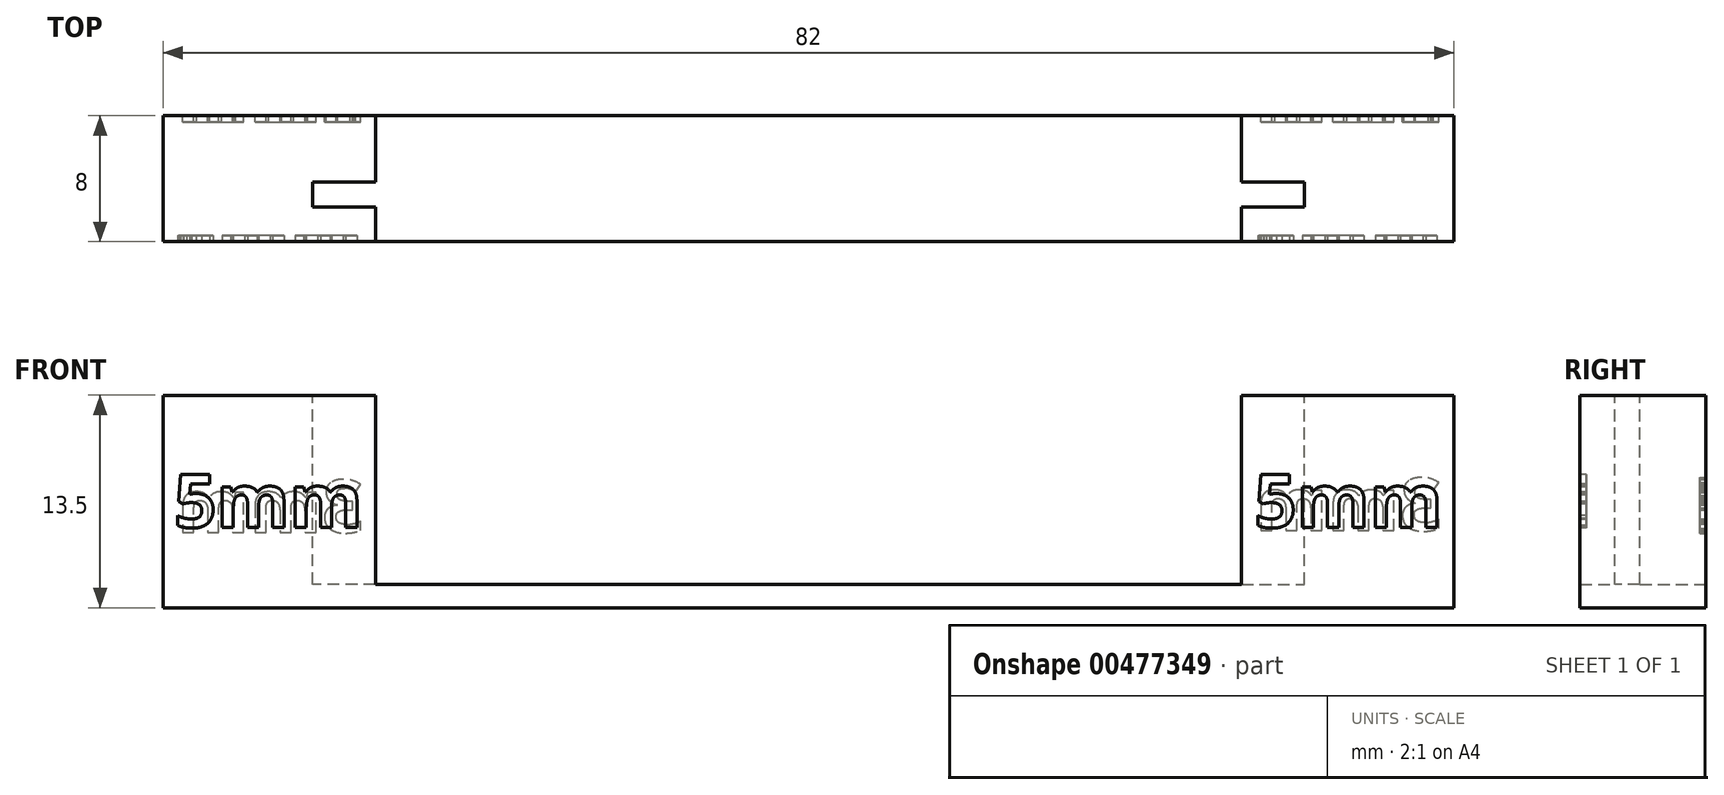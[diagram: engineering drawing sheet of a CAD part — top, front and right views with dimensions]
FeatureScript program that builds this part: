
annotation { "Feature Type Name" : "Feature", "Feature Type Description" : "" }
export const myFeature = defineFeature(function(context is Context, id is Id, definition is map)
    precondition{}
    {
        {
            var Q0;
            Q0=qCreatedBy(makeId("Front.planeOp"),FACE);
            var sketch = newSketch(context, id + "F0", { "sketchPlane" : qUnion([Q0])});
            skLineSegment(sketch, "E0.bottom", {"start": v(-137.41, 25.8) * mm, "end": v(-123.91, 25.8) * mm});
            skLineSegment(sketch, "E0.top", {"start": v(-137.41, 12.3) * mm, "end": v(-123.91, 12.3) * mm});
            skLineSegment(sketch, "E0.left", {"start": v(-137.41, 25.8) * mm, "end": v(-137.41, 12.3) * mm});
            skLineSegment(sketch, "E0.right", {"start": v(-123.91, 25.8) * mm, "end": v(-123.91, 12.3) * mm});
            skLineSegment(sketch, "E1.bottom", {"start": v(-123.91, 12.3) * mm, "end": v(-68.91, 12.3) * mm});
            skLineSegment(sketch, "E1.top", {"start": v(-123.91, 13.8) * mm, "end": v(-68.91, 13.8) * mm});
            skLineSegment(sketch, "E1.left", {"start": v(-123.91, 12.3) * mm, "end": v(-123.91, 13.8) * mm});
            skLineSegment(sketch, "E1.right", {"start": v(-68.91, 12.3) * mm, "end": v(-68.91, 13.8) * mm});
            skLineSegment(sketch, "E2.bottom", {"start": v(-68.91, 12.3) * mm, "end": v(-55.41, 12.3) * mm});
            skLineSegment(sketch, "E2.top", {"start": v(-68.91, 25.8) * mm, "end": v(-55.41, 25.8) * mm});
            skLineSegment(sketch, "E2.left", {"start": v(-68.91, 12.3) * mm, "end": v(-68.91, 25.8) * mm});
            skLineSegment(sketch, "E2.right", {"start": v(-55.41, 12.3) * mm, "end": v(-55.41, 25.8) * mm});
            skSolve(sketch);
        }
        {
            var Q0;
            Q0 = qSketchRegion(id + "F0", true);
            extrude(context, id + "F1", {"entities" : qUnion([Q0]), "depth" : 8 * mm});
        }
        {
            var Q0;
            Q0=makeQuery(id+"F1.opExtrude","SWEPT_FACE",FACE,{"disambiguationData":[OSD([sQuery(id+"F0.wireOp",EDGE,"E0.bottom")])]});
            var sketch = newSketch(context, id + "F2", { "sketchPlane" : qUnion([Q0])});
            skLineSegment(sketch, "E3.bottom", {"start": v(-123.91, -4.2) * mm, "end": v(-127.91, -4.2) * mm});
            skLineSegment(sketch, "E3.top", {"start": v(-123.91, -5.8) * mm, "end": v(-127.91, -5.8) * mm});
            skLineSegment(sketch, "E3.left", {"start": v(-123.91, -4.2) * mm, "end": v(-123.91, -5.8) * mm});
            skLineSegment(sketch, "E3.right", {"start": v(-127.91, -4.2) * mm, "end": v(-127.91, -5.8) * mm});
            skSolve(sketch);
        }
        {
            var Q0;
            Q0=makeQuery(id+"F2.imprint","IMPRINT",FACE,{"disambiguationData":[TD([[makeQuery(id+"F2.imprint","IMPRINT",EDGE,{"derivedFrom":sQuery(id+"F2.wireOp",EDGE,"E3.bottom")}),1.0]])]});
            extrude(context, id + "F3", {"entities" : qUnion([Q0]), "operationType" : NewBodyOperationType.REMOVE, "oppositeDirection" : true, "depth" : 12 * mm});
        }
        {
            var Q0;
            Q0=makeQuery(id+"F1.opExtrude","SWEPT_FACE",FACE,{"disambiguationData":[OSD([sQuery(id+"F0.wireOp",EDGE,"E2.top")])]});
            var sketch = newSketch(context, id + "F4", { "sketchPlane" : qUnion([Q0])});
            skLineSegment(sketch, "E4.bottom", {"start": v(-68.91, -4.2) * mm, "end": v(-64.91, -4.2) * mm});
            skLineSegment(sketch, "E4.top", {"start": v(-68.91, -5.8) * mm, "end": v(-64.91, -5.8) * mm});
            skLineSegment(sketch, "E4.left", {"start": v(-68.91, -4.2) * mm, "end": v(-68.91, -5.8) * mm});
            skLineSegment(sketch, "E4.right", {"start": v(-64.91, -4.2) * mm, "end": v(-64.91, -5.8) * mm});
            skSolve(sketch);
        }
        {
            var Q0;
            Q0 = qSketchRegion(id + "F4", true);
            extrude(context, id + "F5", {"entities" : qUnion([Q0]), "operationType" : NewBodyOperationType.REMOVE, "oppositeDirection" : true, "depth" : 12 * mm});
        }
        {
            var Q0;
            Q0=makeQuery(id+"F1.opExtrude","CAP_FACE",FACE,{"disambiguationData":[OSD([sQuery(id+"F0.wireOp",EDGE,"E0.bottom"),sQuery(id+"F0.wireOp",EDGE,"E0.top"),sQuery(id+"F0.wireOp",EDGE,"E0.left"),sQuery(id+"F0.wireOp",EDGE,"E0.right"),sQuery(id+"F0.wireOp",EDGE,"E1.bottom"),sQuery(id+"F0.wireOp",EDGE,"E1.top"),sQuery(id+"F0.wireOp",EDGE,"E2.bottom"),sQuery(id+"F0.wireOp",EDGE,"E2.top"),sQuery(id+"F0.wireOp",EDGE,"E2.left"),sQuery(id+"F0.wireOp",EDGE,"E2.right")])],"isStart":true});
            var sketch = newSketch(context, id + "F6", { "sketchPlane" : qUnion([Q0])});
            skText(sketch, "E5", { "text": "3mm", "fontName": "OpenSans-Bold.ttf"});
            skText(sketch, "E6", { "text": "3mm", "fontName": "OpenSans-Bold.ttf"});
            const initialGuessF6  = {"E5": [0.0562, 0.0172, 1, 0, 0.00336], "E6": [0.12467, 0.01708, 1, 0, 0.00336]};
            skSetInitialGuess(sketch, initialGuessF6);
            skSolve(sketch);
        }
        {
            var Q0;
            Q0 = qSketchRegion(id + "F6", true);
            extrude(context, id + "F7", {"entities" : qUnion([Q0]), "operationType" : NewBodyOperationType.REMOVE, "oppositeDirection" : true, "depth" : 0.4 * mm});
        }
        {
            var Q0;
            Q0=makeQuery(id+"F1.opExtrude","CAP_FACE",FACE,{"disambiguationData":[OSD([sQuery(id+"F0.wireOp",EDGE,"E0.bottom"),sQuery(id+"F0.wireOp",EDGE,"E0.top"),sQuery(id+"F0.wireOp",EDGE,"E0.left"),sQuery(id+"F0.wireOp",EDGE,"E0.right"),sQuery(id+"F0.wireOp",EDGE,"E1.bottom"),sQuery(id+"F0.wireOp",EDGE,"E1.top"),sQuery(id+"F0.wireOp",EDGE,"E2.bottom"),sQuery(id+"F0.wireOp",EDGE,"E2.top"),sQuery(id+"F0.wireOp",EDGE,"E2.left"),sQuery(id+"F0.wireOp",EDGE,"E2.right")])],"isStart":false});
            var sketch = newSketch(context, id + "F8", { "sketchPlane" : qUnion([Q0])});
            skText(sketch, "E7", { "text": "5mm", "fontName": "OpenSans-Bold.ttf"});
            skText(sketch, "E8", { "text": "5mm", "fontName": "OpenSans-Bold.ttf"});
            const initialGuessF8  = {"E7": [-0.13671, 0.0174, 1, 0, 0.0034], "E8": [-0.06811, 0.0174, 1, 0, 0.0034]};
            skSetInitialGuess(sketch, initialGuessF8);
            skSolve(sketch);
        }
        {
            var Q0;
            Q0 = qSketchRegion(id + "F8", true);
            extrude(context, id + "F9", {"entities" : qUnion([Q0]), "operationType" : NewBodyOperationType.REMOVE, "oppositeDirection" : true, "depth" : 0.4 * mm});
        }
    });
